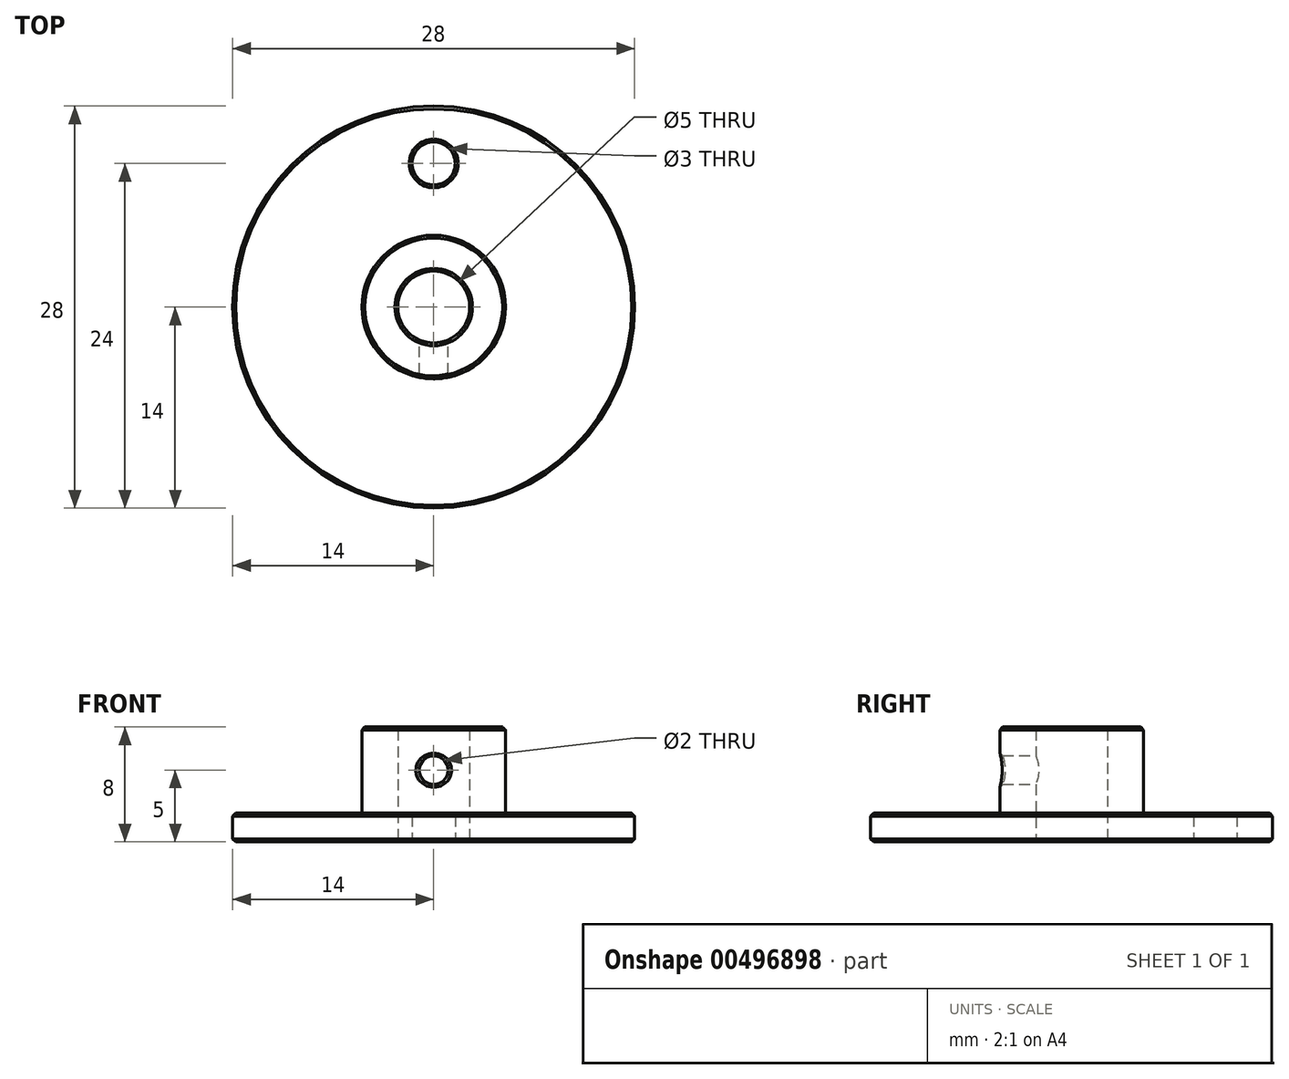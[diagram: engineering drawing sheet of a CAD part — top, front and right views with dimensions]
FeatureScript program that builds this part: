
annotation { "Feature Type Name" : "Feature", "Feature Type Description" : "" }
export const myFeature = defineFeature(function(context is Context, id is Id, definition is map)
    precondition{}
    {
        {
            var Q0;
            Q0=qCreatedBy(makeId("Top.planeOp"),FACE);
            var sketch = newSketch(context, id + "F0", { "sketchPlane" : qUnion([Q0])});
            skCircle(sketch, "E0", {"center": v(0, 0) * mm, "radius": 14 * mm});
            skCircle(sketch, "E1", {"center": v(0, 0) * mm, "radius": 5 * mm});
            skCircle(sketch, "E2", {"center": v(0, 0) * mm, "radius": 2.5 * mm});
            skCircle(sketch, "E3", {"center": v(0, 10) * mm, "radius": 1.5 * mm});
            skSolve(sketch);
        }
        {
            var Q0;
            Q0=makeQuery(id+"F0.imprint","IMPRINT",FACE,{"disambiguationData":[TD([[makeQuery(id+"F0.imprint","IMPRINT",EDGE,{"derivedFrom":sQuery(id+"F0.wireOp",EDGE,"E1")}),1.0]])]});
            extrude(context, id + "F1", {"entities" : qUnion([Q0]), "depth" : 8 * mm});
        }
        {
            var Q0;
            Q0 = qSketchRegion(id + "F0", true);
            extrude(context, id + "F2", {"entities" : qUnion([Q0]), "operationType" : NewBodyOperationType.ADD, "depth" : 2 * mm});
        }
        {
            var Q0;
            Q0=qCreatedBy(makeId("Front.planeOp"),FACE);
            var sketch = newSketch(context, id + "F3", { "sketchPlane" : qUnion([Q0])});
            skCircle(sketch, "E4", {"center": v(0, 5) * mm, "radius": 1 * mm});
            skSolve(sketch);
        }
        {
            var Q0;
            Q0 = qSketchRegion(id + "F3", true);
            var Q1;
            Q1=makeQuery(id+"F3.imprint","IMPRINT",FACE,{"disambiguationData":[TD([[makeQuery(id+"F3.imprint","IMPRINT",EDGE,{"derivedFrom":sQuery(id+"F3.wireOp",EDGE,"E4")}),1.0]])]});
            extrude(context, id + "F4", {"entities" : qUnion([Q0, Q1]), "operationType" : NewBodyOperationType.REMOVE, "oppositeDirection" : true, "depth" : -5 * mm});
        }
        {
            var Q0;
            Q0=makeQuery(id+"F1.opExtrude","CAP_EDGE",EDGE,{"disambiguationData":[OSD([sQuery(id+"F0.wireOp",EDGE,"E1")])],"isStart":false});
            var Q1;
            Q1=makeQuery(id+"F2.opExtrude","CAP_EDGE",EDGE,{"disambiguationData":[OSD([sQuery(id+"F0.wireOp",EDGE,"E0")])],"isStart":false});
            var Q2;
            Q2=makeQuery(id+"F2.opExtrude","CAP_EDGE",EDGE,{"disambiguationData":[OSD([sQuery(id+"F0.wireOp",EDGE,"E0")])],"isStart":true});
            var Q3;
            Q3=makeQuery(id+"F4.boolean.opBoolean","INTERSECT",EDGE,{"derivedFrom":[makeQuery(id+"F1.opExtrude","SWEPT_FACE",FACE,{"disambiguationData":[OSD([sQuery(id+"F0.wireOp",EDGE,"E1")])]}),makeQuery(id+"F4.opExtrude","SWEPT_FACE",FACE,{"disambiguationData":[OSD([sQuery(id+"F3.wireOp",EDGE,"E4")])]})]});
            var Q4;
            Q4=makeQuery(id+"F1.opExtrude","CAP_EDGE",EDGE,{"disambiguationData":[OSD([sQuery(id+"F0.wireOp",EDGE,"E2")])],"isStart":false});
            var Q5;
            Q5=makeQuery(id+"F2.opExtrude","CAP_EDGE",EDGE,{"disambiguationData":[OSD([sQuery(id+"F0.wireOp",EDGE,"E3")])],"isStart":false});
            var Q6;
            Q6=makeQuery(id+"F1.opExtrude","CAP_EDGE",EDGE,{"disambiguationData":[OSD([sQuery(id+"F0.wireOp",EDGE,"E2")])],"isStart":true});
            var Q7;
            Q7=makeQuery(id+"F2.opExtrude","CAP_EDGE",EDGE,{"disambiguationData":[OSD([sQuery(id+"F0.wireOp",EDGE,"E3")])],"isStart":true});
            chamfer(context, id + "F5", {"entities" : qUnion([Q0, Q1, Q2, Q3, Q4, Q5, Q6, Q7]), "width" : 0.2 * mm, "tangentPropagation" : true});
        }
    });
